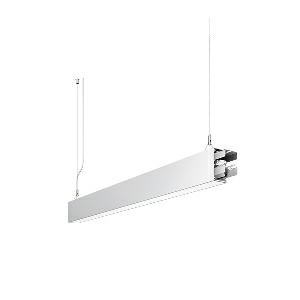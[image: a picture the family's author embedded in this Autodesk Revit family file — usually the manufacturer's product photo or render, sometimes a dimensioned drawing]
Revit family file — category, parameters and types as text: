
# Revit family: idoo_line_-_ilp_2000_840_d_sta_00805680_f679
name_source: partatom
category: Lighting Fixtures
units: mm (PartAtom-declared; Revit-internal decimal feet)

## family parameters
Cut with Voids When Loaded = No
Host = Face
Light Source = No
Part Type = Normal
Room Calculation Point = No
Round Connector Dimension = Use Diameter
Shared = No

## types (1)
- IDOO.line - ILP 2000/840/D STA (1 x LED, 2350 lm, 4000K)
    Apparent Load = 17 VA
    Approval mark = CE
    CIE Flux Codes = 66 91 98 40 100
    Color Rendering = 80-89
    Color Temperature = 4000K
    Control Gear = Electronic ballast
    Default Elevation = 1800 mm
    Description = ILP 2000/840/D|Suspended luminaire|light source: LED|connected load: 220-240 V, 50/60 Hz|Power consumption: approx. 17 W|standby: approx. 0,20|luminous flux: 2350 lm|luminous efficacy: 138 lm/W|light distribution: Direct/indirect|direct ratio: approx. 40 %|colour temperature: Cold white, ca. 4000 K|color rendering index (CRI): >= 80|chromaticity tolerance:  3 SDCM|System of protection: IP 40|technology: Continuously dimmable|luminaire body|material: Sectional aluminium|colour: White|lamp cover: Acrylic (PMMA), Clear|mains lead: 2.00 m With free stranded wires|Fastening: Steel cable 0.3 - 0.7 m|glare control: Prism aperture|luminance(L65): <= 2700 cd/m|unified glare rating(4H 8H): <=  16|special features: DALI Load 1x, TouchDIM - dimming via standard switch, Through-wired, up to 18 m on one mains connection, Flicker-free, Suitable as emergency lighting, Start luminaire with mains connection, Mechanical and electrical connection of the individual modules without tools|
    Frequency = 50 Hz
    Height = 110 mm
    Lamp = 1 x LED
    Lamp Light Flux = 2350 lm
    Lamp count = 1
    Length = 848 mm
    Luminous efficacy = 138 lm/W
    Manufacturer = Waldmann
    ModVariant = No
    Model = 00805680
    Mounting Place = Ceiling
    Mounting Type = Pendant
    Number of Poles = 1
    OnlyDefault = Yes
    Power Factor = 1
    Product Name = IDOO.line - ILP 2000/840/D STA
    Product group = Suspended luminaire
    ProductGroupID = 9
    Protection Class = Protection class I
    Protection Degree = IP 40
    RLX_Detail_Level = 1
    RLX_Emergency_Light_Flux = 0 lm
    RLX_Emergency_Type = 0
    RLX_Emergency_Type_DB = No
    RlxData = <blob elided: 19413 chars, md5=45339b19>
    Socket = socket
    Standby Power = 0 W
    System Light Flux = 2350 lm
    System Power = 17 W
    Type Comments = Product without accessories
    Type Image = 113295000-00692543.jpg
    URL = http://relux.com
    VarID = ---
    Voltage = 230 V
    Voltage Range = 220-240 V
    Weight = 0.00 kg
    Width = 60 mm  [stored 0.19685 ft]

note: [stored X ft] marks values corroborated as IEEE doubles in the binary element streams (Revit-internal decimal feet)

## geometry (parser evidence)
native form markers: Blend x4, Sweep x12
no freeform markers — native parametric forms only
